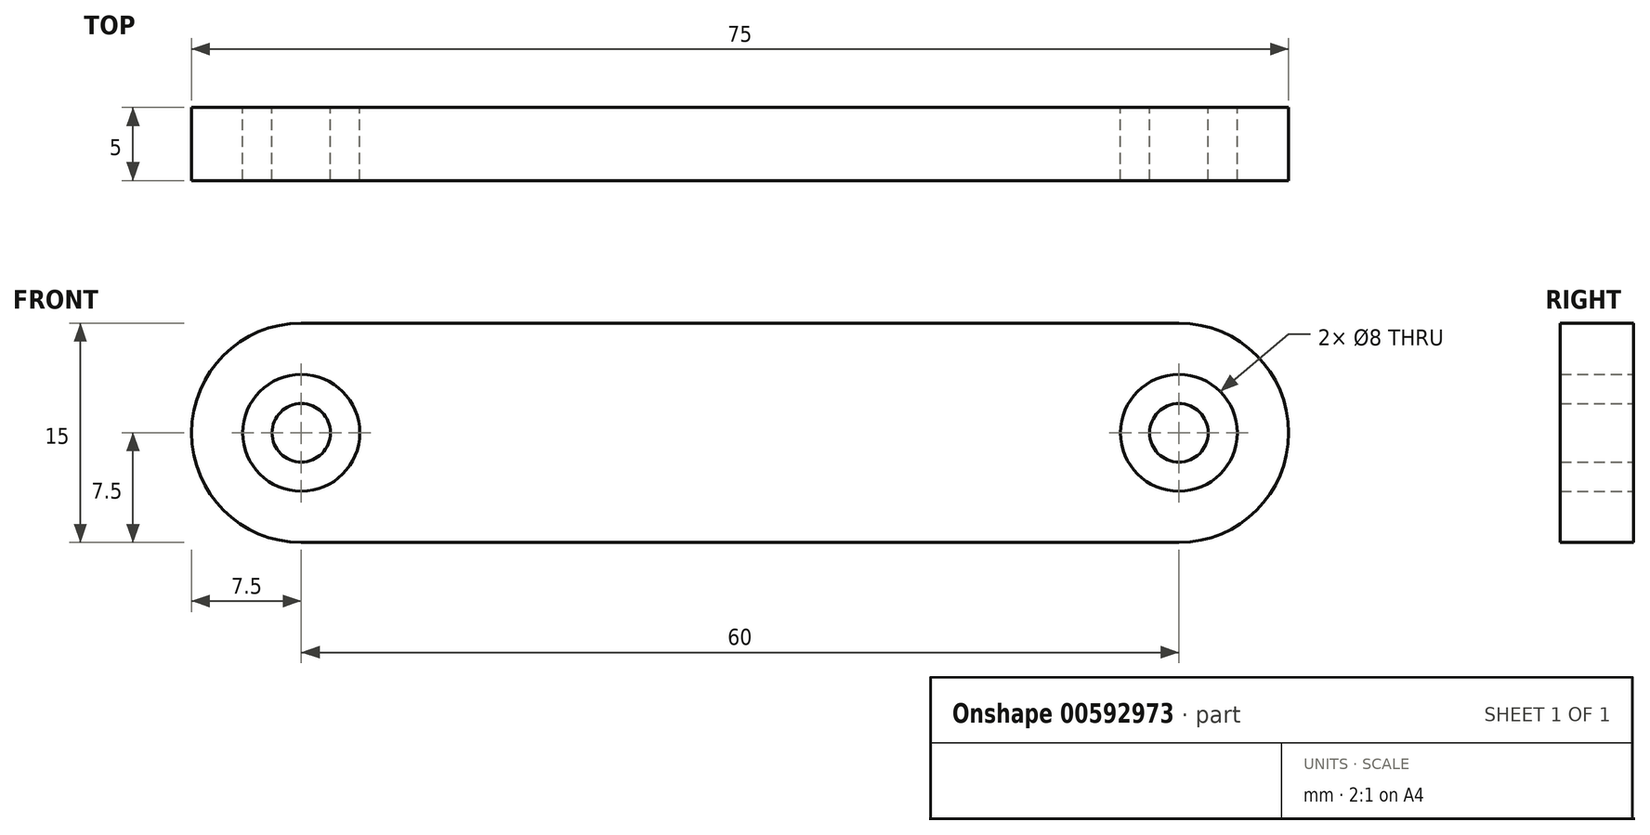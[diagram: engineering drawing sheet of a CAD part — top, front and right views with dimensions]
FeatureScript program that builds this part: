
annotation { "Feature Type Name" : "Feature", "Feature Type Description" : "" }
export const myFeature = defineFeature(function(context is Context, id is Id, definition is map)
    precondition{}
    {
        {
            var Q0;
            Q0=qCreatedBy(makeId("Front.planeOp"),FACE);
            var sketch = newSketch(context, id + "F0", { "sketchPlane" : qUnion([Q0])});
            skCircle(sketch, "E0", {"center": v(0, 0) * mm, "radius": 7.5 * mm});
            skCircle(sketch, "E1", {"center": v(60, 0) * mm, "radius": 7.5 * mm});
            skCircle(sketch, "E2", {"center": v(0, 0) * mm, "radius": 4 * mm});
            skCircle(sketch, "E3", {"center": v(60, 0) * mm, "radius": 4 * mm});
            skCircle(sketch, "E4", {"center": v(60, 0) * mm, "radius": 2 * mm});
            skCircle(sketch, "E5", {"center": v(0, 0) * mm, "radius": 2 * mm});
            skLineSegment(sketch, "E6", {"start": v(0, 7.5) * mm, "end": v(60, 7.5) * mm});
            skLineSegment(sketch, "E7", {"start": v(0, -7.5) * mm, "end": v(60, -7.5) * mm});
            skSolve(sketch);
        }
        {
            var Q0;
            Q0=makeQuery(id+"F0.imprint","IMPRINT",FACE,{"disambiguationData":[TD([[makeQuery(id+"F0.imprint","IMPRINT",EDGE,{"derivedFrom":sQuery(id+"F0.wireOp",EDGE,"E2")}),-1.0]])]});
            var Q1;
            {var subQ0=sQuery(id+"F0.wireOp",EDGE,"E6");Q1=makeQuery(id+"F0.imprint","IMPRINT",FACE,{"disambiguationData":[TD([[makeQuery(id+"F0.imprint","IMPRINT",EDGE,{"derivedFrom":subQ0}),-1.0]])]});}
            var Q2;
            Q2=makeQuery(id+"F0.imprint","IMPRINT",FACE,{"disambiguationData":[TD([[makeQuery(id+"F0.imprint","IMPRINT",EDGE,{"derivedFrom":sQuery(id+"F0.wireOp",EDGE,"E3")}),-1.0]])]});
            var Q3;
            Q3=makeQuery(id+"F0.imprint","IMPRINT",FACE,{"disambiguationData":[TD([[makeQuery(id+"F0.imprint","IMPRINT",EDGE,{"derivedFrom":sQuery(id+"F0.wireOp",EDGE,"E4")}),1.0]])]});
            var Q4;
            Q4=makeQuery(id+"F0.imprint","IMPRINT",FACE,{"disambiguationData":[TD([[makeQuery(id+"F0.imprint","IMPRINT",EDGE,{"derivedFrom":sQuery(id+"F0.wireOp",EDGE,"E5")}),1.0]])]});
            extrude(context, id + "F1", {"entities" : qUnion([Q0, Q1, Q2, Q3, Q4]), "depth" : 5 * mm, "offsetDistance" : 25 * mm});
        }
    });
